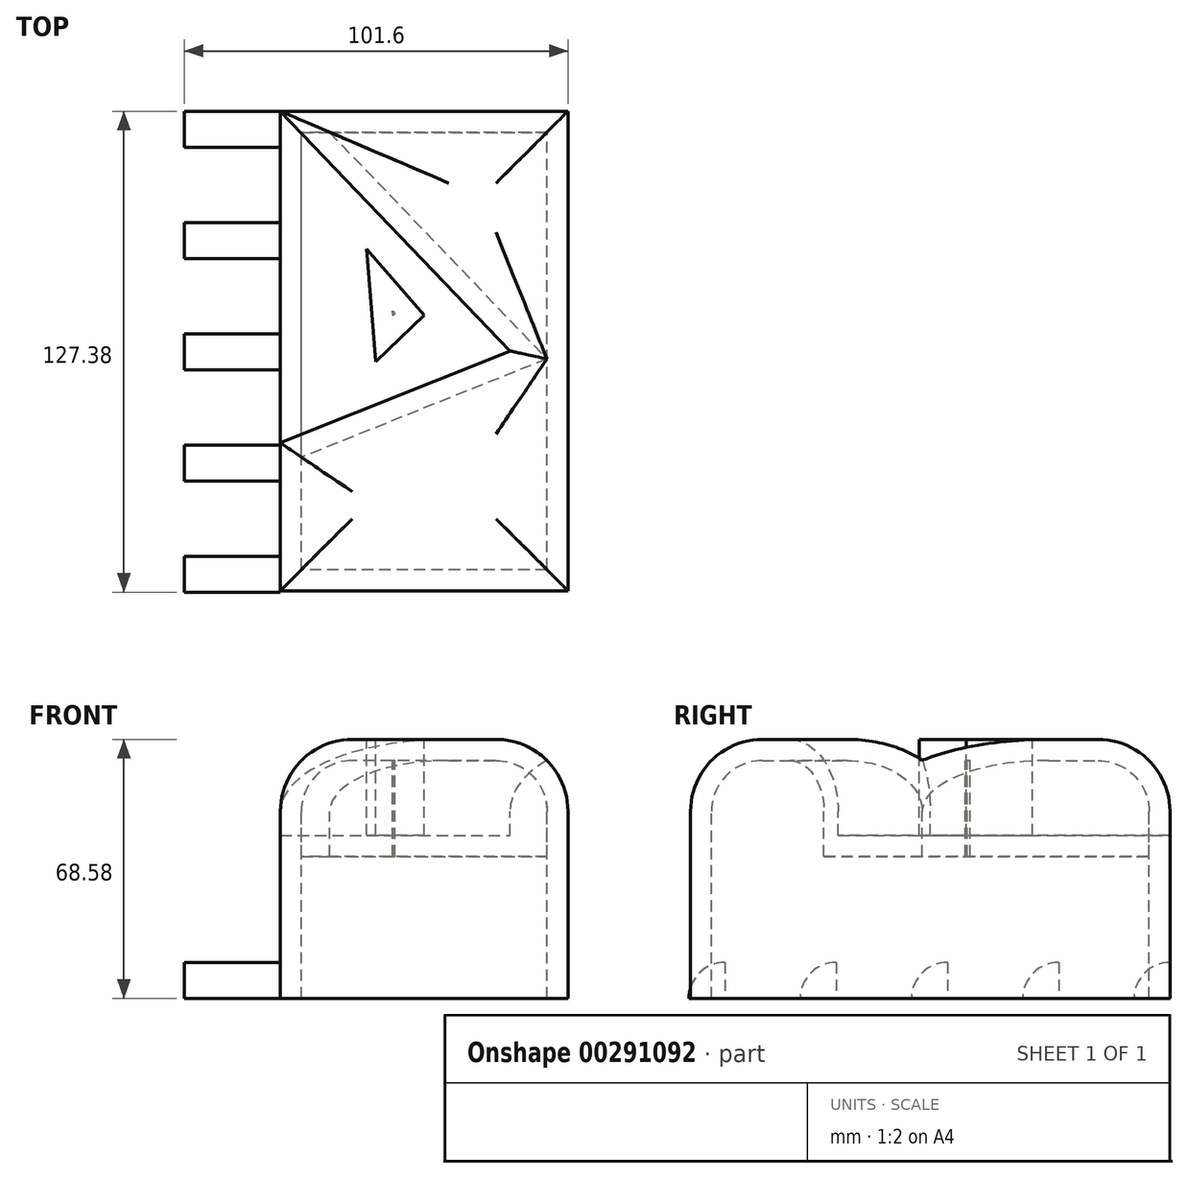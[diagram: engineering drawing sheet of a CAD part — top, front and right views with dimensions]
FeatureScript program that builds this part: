
annotation { "Feature Type Name" : "Feature", "Feature Type Description" : "" }
export const myFeature = defineFeature(function(context is Context, id is Id, definition is map)
    precondition{}
    {
        {
            var Q0;
            Q0=qCreatedBy(makeId("Top.planeOp"),FACE);
            var sketch = newSketch(context, id + "F0", { "sketchPlane" : qUnion([Q0])});
            skLineSegment(sketch, "E0.bottom", {"start": v(38.1, -63.5) * mm, "end": v(-38.1, -63.5) * mm});
            skLineSegment(sketch, "E0.top", {"start": v(38.1, 63.5) * mm, "end": v(-38.1, 63.5) * mm});
            skLineSegment(sketch, "E0.left", {"start": v(38.1, -63.5) * mm, "end": v(38.1, 63.5) * mm});
            skLineSegment(sketch, "E0.right", {"start": v(-38.1, -63.5) * mm, "end": v(-38.1, 63.5) * mm});
            skPoint(sketch, "E0.middle", {"position": v(0, 0) * mm});
            skSolve(sketch);
        }
        {
            var Q0;
            Q0 = qSketchRegion(id + "F0", true);
            extrude(context, id + "F1", {"entities" : qUnion([Q0]), "oppositeDirection" : true, "depth" : 43.18 * mm, "hasSecondDirection" : true, "secondDirectionOppositeDirection" : false, "secondDirectionDepth" : 25.4 * mm});
        }
        {
            var Q0;
            Q0=makeQuery(id+"F1.opExtrude","CAP_FACE",FACE,{"disambiguationData":[OSD([sQuery(id+"F0.wireOp",EDGE,"E0.bottom"),sQuery(id+"F0.wireOp",EDGE,"E0.top"),sQuery(id+"F0.wireOp",EDGE,"E0.left"),sQuery(id+"F0.wireOp",EDGE,"E0.right")])],"isStart":true});
            var sketch = newSketch(context, id + "F2", { "sketchPlane" : qUnion([Q0])});
            skLineSegment(sketch, "E1", {"start": v(-38.1, 63.5) * mm, "end": v(22.73, 0) * mm});
            skLineSegment(sketch, "E2", {"start": v(22.73, 0) * mm, "end": v(-38.1, -24.37) * mm});
            skLineSegment(sketch, "E3", {"start": v(-38.1, -24.37) * mm, "end": v(-38.1, 63.5) * mm});
            skLineSegment(sketch, "E4", {"start": v(-15.26, 27) * mm, "end": v(0, 9.48) * mm});
            skLineSegment(sketch, "E5", {"start": v(0, 9.48) * mm, "end": v(-12.88, -2.87) * mm});
            skLineSegment(sketch, "E6", {"start": v(-12.88, -2.87) * mm, "end": v(-15.26, 27) * mm});
            skLineSegment(sketch, "E7", {"start": v(-38.1, 63.5) * mm, "end": v(-38.1, -24.37) * mm});
            skSolve(sketch);
        }
        {
            var Q0;
            Q0 = qSketchRegion(id + "F2", true);
            var Q1;
            Q1=makeQuery(id+"F1.opExtrude","CAP_FACE",FACE,{"disambiguationData":[OSD([sQuery(id+"F0.wireOp",EDGE,"E0.bottom"),sQuery(id+"F0.wireOp",EDGE,"E0.top"),sQuery(id+"F0.wireOp",EDGE,"E0.left"),sQuery(id+"F0.wireOp",EDGE,"E0.right")])],"isStart":false});
            extrude(context, id + "F3", {"entities" : qUnion([Q0]), "operationType" : NewBodyOperationType.REMOVE, "oppositeDirection" : true, "depth" : 25.4 * mm});
        }
        {
            var Q0;
            {var subQ0=sQuery(id+"F0.wireOp",EDGE,"E0.left");var subQ1=sQuery(id+"F0.wireOp",EDGE,"E0.top");var subQ2=sQuery(id+"F0.wireOp",EDGE,"E0.right");var subQ3=sQuery(id+"F0.wireOp",EDGE,"E0.bottom");Q0=makeQuery(id+"F3.boolean.opBoolean","SPLIT",FACE,{"disambiguationData":[TD([makeQuery(id+"F1.opExtrude","SWEPT_FACE",FACE,{"disambiguationData":[OSD([subQ3])]})])],"derivedFrom":makeQuery(id+"F1.opExtrude","CAP_FACE",FACE,{"disambiguationData":[OSD([subQ3,subQ1,subQ0,subQ2])],"isStart":true})});}
            fillet(context, id + "F4", {"entities" : qUnion([Q0]), "radius" : 19.05 * mm, "tangentPropagation" : true, "allowEdgeOverflow" : false});
        }
        {
            var Q0;
            Q0=makeQuery(id+"F1.opExtrude","CAP_FACE",FACE,{"disambiguationData":[OSD([sQuery(id+"F0.wireOp",EDGE,"E0.bottom"),sQuery(id+"F0.wireOp",EDGE,"E0.top"),sQuery(id+"F0.wireOp",EDGE,"E0.left"),sQuery(id+"F0.wireOp",EDGE,"E0.right")])],"isStart":false});
            shell(context, id + "F5", {"entities" : qUnion([Q0]), "thickness" : 5.6 * mm});
        }
        {
            var Q0;
            Q0=makeQuery(id+"F1.opExtrude","SWEPT_FACE",FACE,{"disambiguationData":[OSD([sQuery(id+"F0.wireOp",EDGE,"E0.right")])]});
            var sketch = newSketch(context, id + "F6", { "sketchPlane" : qUnion([Q0])});
            skArc(sketch, "E8", {"start": v(-53.98, -43.18) * mm, "mid": v(-56.76, -36.44) * mm, "end": v(-63.5, -33.65) * mm});
            skLineSegment(sketch, "E9", {"start": v(-63.5, -33.65) * mm, "end": v(-63.5, -43.18) * mm});
            skLineSegment(sketch, "E10", {"start": v(-53.98, -43.18) * mm, "end": v(-63.5, -43.18) * mm});
            skArc(sketch, "E11.1.0.0", {"start": v(-24.51, -43.18) * mm, "mid": v(-27.3, -36.44) * mm, "end": v(-34.04, -33.65) * mm});
            skLineSegment(sketch, "E11.1.0.1", {"start": v(-34.04, -33.65) * mm, "end": v(-34.04, -43.18) * mm});
            skLineSegment(sketch, "E11.1.0.2", {"start": v(-24.51, -43.18) * mm, "end": v(-34.04, -43.18) * mm});
            skArc(sketch, "E11.2.0.0", {"start": v(4.95, -43.18) * mm, "mid": v(2.16, -36.44) * mm, "end": v(-4.57, -33.65) * mm});
            skLineSegment(sketch, "E11.2.0.1", {"start": v(-4.57, -33.65) * mm, "end": v(-4.57, -43.18) * mm});
            skLineSegment(sketch, "E11.2.0.2", {"start": v(4.95, -43.18) * mm, "end": v(-4.57, -43.18) * mm});
            skArc(sketch, "E11.3.0.0", {"start": v(34.42, -43.18) * mm, "mid": v(31.63, -36.44) * mm, "end": v(24.9, -33.65) * mm});
            skLineSegment(sketch, "E11.3.0.1", {"start": v(24.9, -33.65) * mm, "end": v(24.9, -43.18) * mm});
            skLineSegment(sketch, "E11.3.0.2", {"start": v(34.42, -43.18) * mm, "end": v(24.9, -43.18) * mm});
            skArc(sketch, "E11.4.0.0", {"start": v(63.88, -43.18) * mm, "mid": v(61.1, -36.44) * mm, "end": v(54.36, -33.65) * mm});
            skLineSegment(sketch, "E11.4.0.1", {"start": v(54.36, -33.65) * mm, "end": v(54.36, -43.18) * mm});
            skLineSegment(sketch, "E11.4.0.2", {"start": v(63.88, -43.18) * mm, "end": v(54.36, -43.18) * mm});
            skLineSegment(sketch, "E11.direction1", {"start": v(-63.5, -43.18) * mm, "end": v(-34.04, -43.18) * mm, "construction": true});
            skSolve(sketch);
        }
        {
            var Q0;
            Q0 = qSketchRegion(id + "F6", true);
            extrude(context, id + "F7", {"entities" : qUnion([Q0]), "operationType" : NewBodyOperationType.ADD, "depth" : 25.4 * mm});
        }
    });
